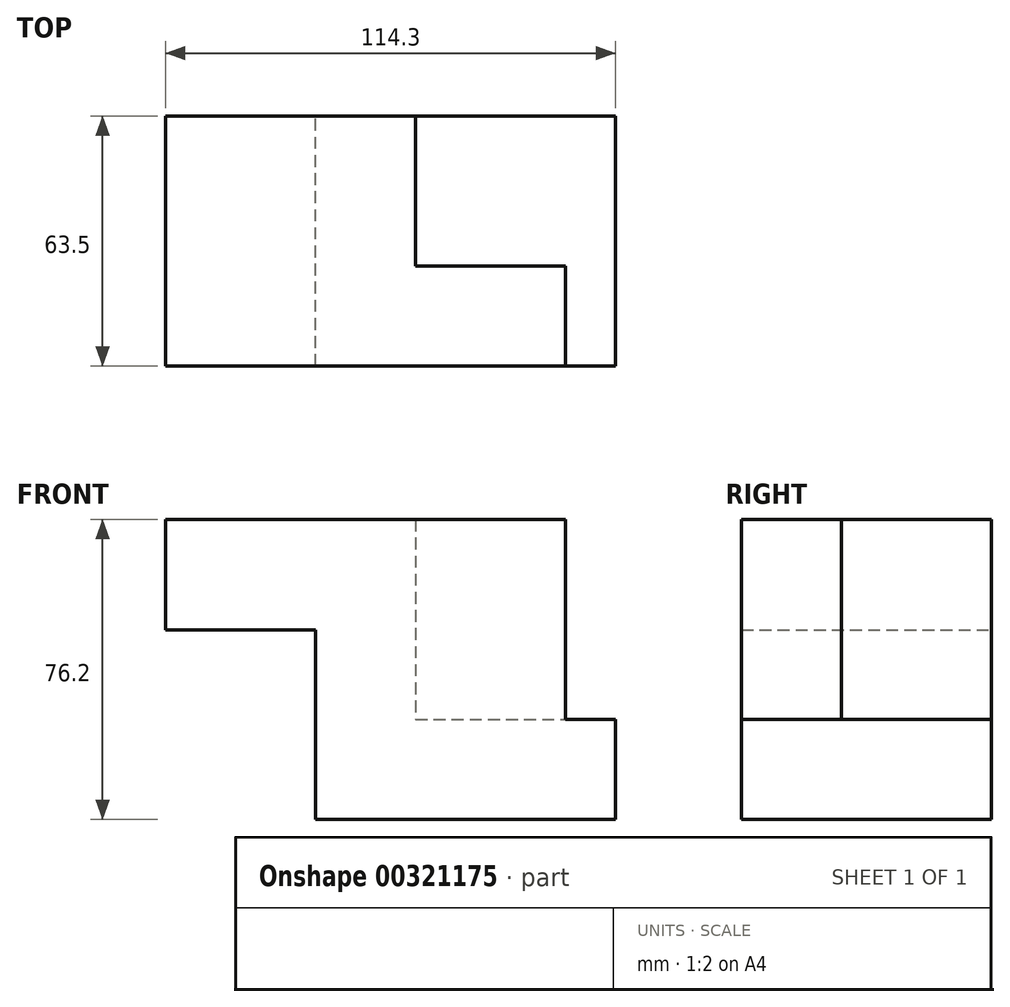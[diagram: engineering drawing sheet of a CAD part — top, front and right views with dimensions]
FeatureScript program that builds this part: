
annotation { "Feature Type Name" : "Feature", "Feature Type Description" : "" }
export const myFeature = defineFeature(function(context is Context, id is Id, definition is map)
    precondition{}
    {
        {
            var Q0;
            Q0=qCreatedBy(makeId("Front.planeOp"),FACE);
            var sketch = newSketch(context, id + "F0", { "sketchPlane" : qUnion([Q0])});
            skLineSegment(sketch, "E0", {"start": v(-10.78, -25.6) * mm, "end": v(-86.98, -25.6) * mm});
            skLineSegment(sketch, "E1", {"start": v(-86.98, -25.6) * mm, "end": v(-86.98, 22.6) * mm});
            skLineSegment(sketch, "E2", {"start": v(-86.98, 22.6) * mm, "end": v(-125.08, 22.6) * mm});
            skLineSegment(sketch, "E3", {"start": v(-125.08, 22.6) * mm, "end": v(-125.08, 50.6) * mm});
            skLineSegment(sketch, "E4", {"start": v(-125.08, 50.6) * mm, "end": v(-86.98, 50.6) * mm});
            skLineSegment(sketch, "E5", {"start": v(-86.98, 50.6) * mm, "end": v(-61.58, 50.6) * mm});
            skLineSegment(sketch, "E6", {"start": v(-61.58, 50.6) * mm, "end": v(-61.58, -0.2) * mm});
            skLineSegment(sketch, "E7", {"start": v(-61.58, -0.2) * mm, "end": v(-10.78, -0.2) * mm});
            skLineSegment(sketch, "E8", {"start": v(-10.78, -0.2) * mm, "end": v(-10.78, -25.6) * mm});
            skSolve(sketch);
        }
        {
            var Q0;
            Q0=makeQuery(id+"F0.imprint","IMPRINT",FACE,{"disambiguationData":[TD([[makeQuery(id+"F0.imprint","IMPRINT",EDGE,{"derivedFrom":sQuery(id+"F0.wireOp",EDGE,"E0")}),-1.0]])]});
            extrude(context, id + "F1", {"entities" : qUnion([Q0]), "depth" : 63.5 * mm});
        }
        {
            var Q0;
            Q0=makeQuery(id+"F1.opExtrude","CAP_FACE",FACE,{"disambiguationData":[OSD([sQuery(id+"F0.wireOp",EDGE,"E0"),sQuery(id+"F0.wireOp",EDGE,"E1"),sQuery(id+"F0.wireOp",EDGE,"E2"),sQuery(id+"F0.wireOp",EDGE,"E3"),sQuery(id+"F0.wireOp",EDGE,"E4"),sQuery(id+"F0.wireOp",EDGE,"E5"),sQuery(id+"F0.wireOp",EDGE,"E6"),sQuery(id+"F0.wireOp",EDGE,"E7"),sQuery(id+"F0.wireOp",EDGE,"E8")])],"isStart":false});
            var sketch = newSketch(context, id + "F2", { "sketchPlane" : qUnion([Q0])});
            skLineSegment(sketch, "E9", {"start": v(-61.58, 50.6) * mm, "end": v(-23.48, 50.6) * mm});
            skLineSegment(sketch, "E10", {"start": v(-23.48, 50.6) * mm, "end": v(-23.48, -0.2) * mm});
            skSolve(sketch);
        }
        {
            var Q0;
            Q0=makeQuery(id+"F2.imprint","IMPRINT",FACE,{"disambiguationData":[TD([[makeQuery(id+"F2.imprint","IMPRINT",EDGE,{"derivedFrom":sQuery(id+"F2.wireOp",EDGE,"E9")}),-1.0]])]});
            extrude(context, id + "F3", {"entities" : qUnion([Q0]), "operationType" : NewBodyOperationType.ADD, "oppositeDirection" : true, "depth" : 25.4 * mm});
        }
    });
